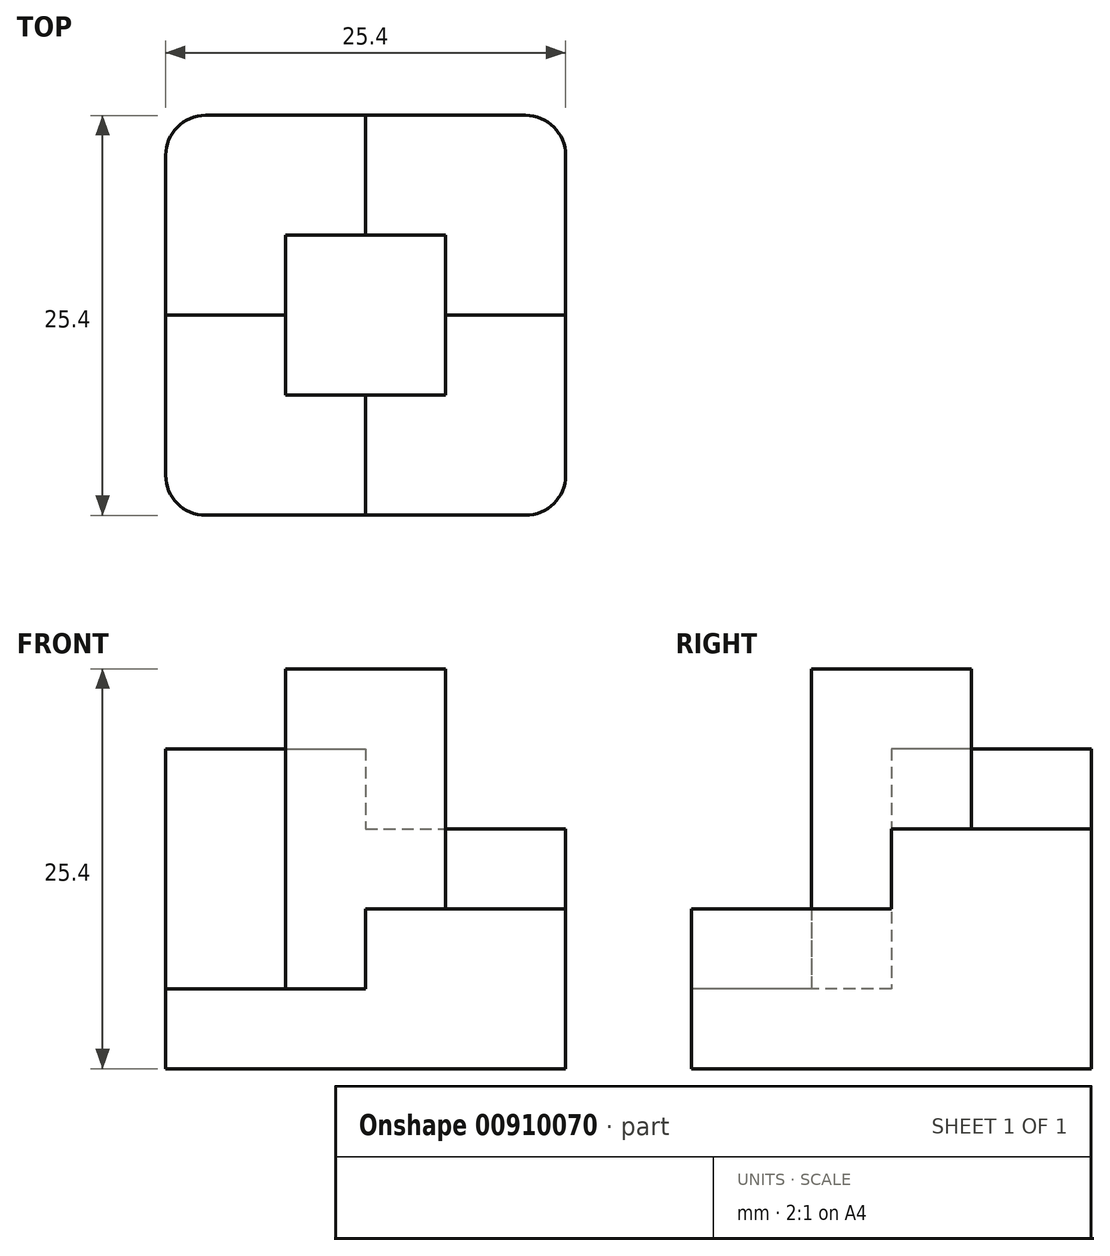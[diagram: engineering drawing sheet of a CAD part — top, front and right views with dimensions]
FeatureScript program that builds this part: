
annotation { "Feature Type Name" : "Feature", "Feature Type Description" : "" }
export const myFeature = defineFeature(function(context is Context, id is Id, definition is map)
    precondition{}
    {
        {
            var Q0;
            Q0=qCreatedBy(makeId("Top.planeOp"),FACE);
            var sketch = newSketch(context, id + "F0", { "sketchPlane" : qUnion([Q0])});
            skLineSegment(sketch, "E0.bottom", {"start": v(-10.88, 13.86) * mm, "end": v(9.44, 13.86) * mm});
            skLineSegment(sketch, "E0.top", {"start": v(-10.88, -11.54) * mm, "end": v(9.44, -11.54) * mm});
            skLineSegment(sketch, "E0.left", {"start": v(-13.42, 11.32) * mm, "end": v(-13.42, -9) * mm});
            skLineSegment(sketch, "E0.right", {"start": v(11.98, 11.32) * mm, "end": v(11.98, -9) * mm});
            skLineSegment(sketch, "E1.bottom", {"start": v(-5.8, 6.24) * mm, "end": v(4.36, 6.24) * mm});
            skLineSegment(sketch, "E1.top", {"start": v(-5.8, -3.92) * mm, "end": v(4.36, -3.92) * mm});
            skLineSegment(sketch, "E1.left", {"start": v(-5.8, 6.24) * mm, "end": v(-5.8, -3.92) * mm});
            skLineSegment(sketch, "E1.right", {"start": v(4.36, 6.24) * mm, "end": v(4.36, -3.92) * mm});
            skLineSegment(sketch, "E2.left", {"start": v(-5.8, -0.26) * mm, "end": v(-5.8, -0.26) * mm});
            skLineSegment(sketch, "E2.right", {"start": v(-13.42, 1.92) * mm, "end": v(-13.42, 1.92) * mm});
            skLineSegment(sketch, "E3", {"start": v(-5.8, 1.16) * mm, "end": v(-13.42, 1.16) * mm});
            skLineSegment(sketch, "E4", {"start": v(4.36, 1.16) * mm, "end": v(11.98, 1.16) * mm});
            skLineSegment(sketch, "E5", {"start": v(-0.72, 6.24) * mm, "end": v(-0.72, 13.86) * mm});
            skLineSegment(sketch, "E6", {"start": v(-0.72, -3.92) * mm, "end": v(-0.72, -11.54) * mm});
            skPoint(sketch, "E7.visualSharp", {"position": v(-13.42, 13.86) * mm});
            skArc(sketch, "E7.filletArc", {"start": v(-10.88, 13.86) * mm, "mid": v(-12.67, 13.12) * mm, "end": v(-13.42, 11.32) * mm});
            skPoint(sketch, "E8.visualSharp", {"position": v(11.98, 13.86) * mm});
            skArc(sketch, "E8.filletArc", {"start": v(11.98, 11.32) * mm, "mid": v(11.24, 13.12) * mm, "end": v(9.44, 13.86) * mm});
            skPoint(sketch, "E9.visualSharp", {"position": v(11.98, -11.54) * mm});
            skArc(sketch, "E9.filletArc", {"start": v(9.44, -11.54) * mm, "mid": v(11.24, -10.8) * mm, "end": v(11.98, -9) * mm});
            skPoint(sketch, "E10.visualSharp", {"position": v(-13.42, -11.54) * mm});
            skArc(sketch, "E10.filletArc", {"start": v(-13.42, -9) * mm, "mid": v(-12.67, -10.8) * mm, "end": v(-10.88, -11.54) * mm});
            skSolve(sketch);
        }
        {
            var Q0;
            {var subQ3=sQuery(id+"F0.wireOp",EDGE,"E3");Q0=makeQuery(id+"F0.imprint","IMPRINT",FACE,{"disambiguationData":[TD([[makeQuery(id+"F0.imprint","IMPRINT",EDGE,{"derivedFrom":subQ3}),-1.0]])]});}
            extrude(context, id + "F1", {"entities" : qUnion([Q0]), "depth" : 20.32 * mm, "offsetDistance" : 25.4 * mm});
        }
        {
            var Q0;
            {var subQ3=sQuery(id+"F0.wireOp",EDGE,"E4");Q0=makeQuery(id+"F0.imprint","IMPRINT",FACE,{"disambiguationData":[TD([[makeQuery(id+"F0.imprint","IMPRINT",EDGE,{"derivedFrom":subQ3}),1.0]])]});}
            extrude(context, id + "F2", {"entities" : qUnion([Q0]), "operationType" : NewBodyOperationType.ADD, "depth" : 15.24 * mm, "offsetDistance" : 25.4 * mm});
        }
        {
            var Q0;
            {var subQ4=sQuery(id+"F0.wireOp",EDGE,"E1.left");var subQ6=sQuery(id+"F0.wireOp",EDGE,"E1.bottom");var subQ9=makeQuery(id+"F0.imprint","INTERSECT",VERTEX,{"derivedFrom":[subQ6,subQ4]});Q0=makeQuery(id+"F0.imprint","IMPRINT",FACE,{"disambiguationData":[TD([[makeQuery(id+"F0.imprint","IMPRINT",EDGE,{"disambiguationData":[TD([[subQ9,-1.0]])],"derivedFrom":subQ6}),-1.0]])]});}
            extrude(context, id + "F3", {"entities" : qUnion([Q0]), "operationType" : NewBodyOperationType.ADD, "depth" : 25.4 * mm, "offsetDistance" : 25.4 * mm});
        }
        {
            var Q0;
            {var subQ3=sQuery(id+"F0.wireOp",EDGE,"E4");Q0=makeQuery(id+"F0.imprint","IMPRINT",FACE,{"disambiguationData":[TD([[makeQuery(id+"F0.imprint","IMPRINT",EDGE,{"derivedFrom":subQ3}),-1.0]])]});}
            extrude(context, id + "F4", {"entities" : qUnion([Q0]), "operationType" : NewBodyOperationType.ADD, "depth" : 10.16 * mm, "offsetDistance" : 25.4 * mm});
        }
        {
            var Q0;
            {var subQ3=sQuery(id+"F0.wireOp",EDGE,"E3");Q0=makeQuery(id+"F0.imprint","IMPRINT",FACE,{"disambiguationData":[TD([[makeQuery(id+"F0.imprint","IMPRINT",EDGE,{"derivedFrom":subQ3}),1.0]])]});}
            extrude(context, id + "F5", {"entities" : qUnion([Q0]), "operationType" : NewBodyOperationType.ADD, "depth" : 5.08 * mm, "offsetDistance" : 25.4 * mm});
        }
    });
